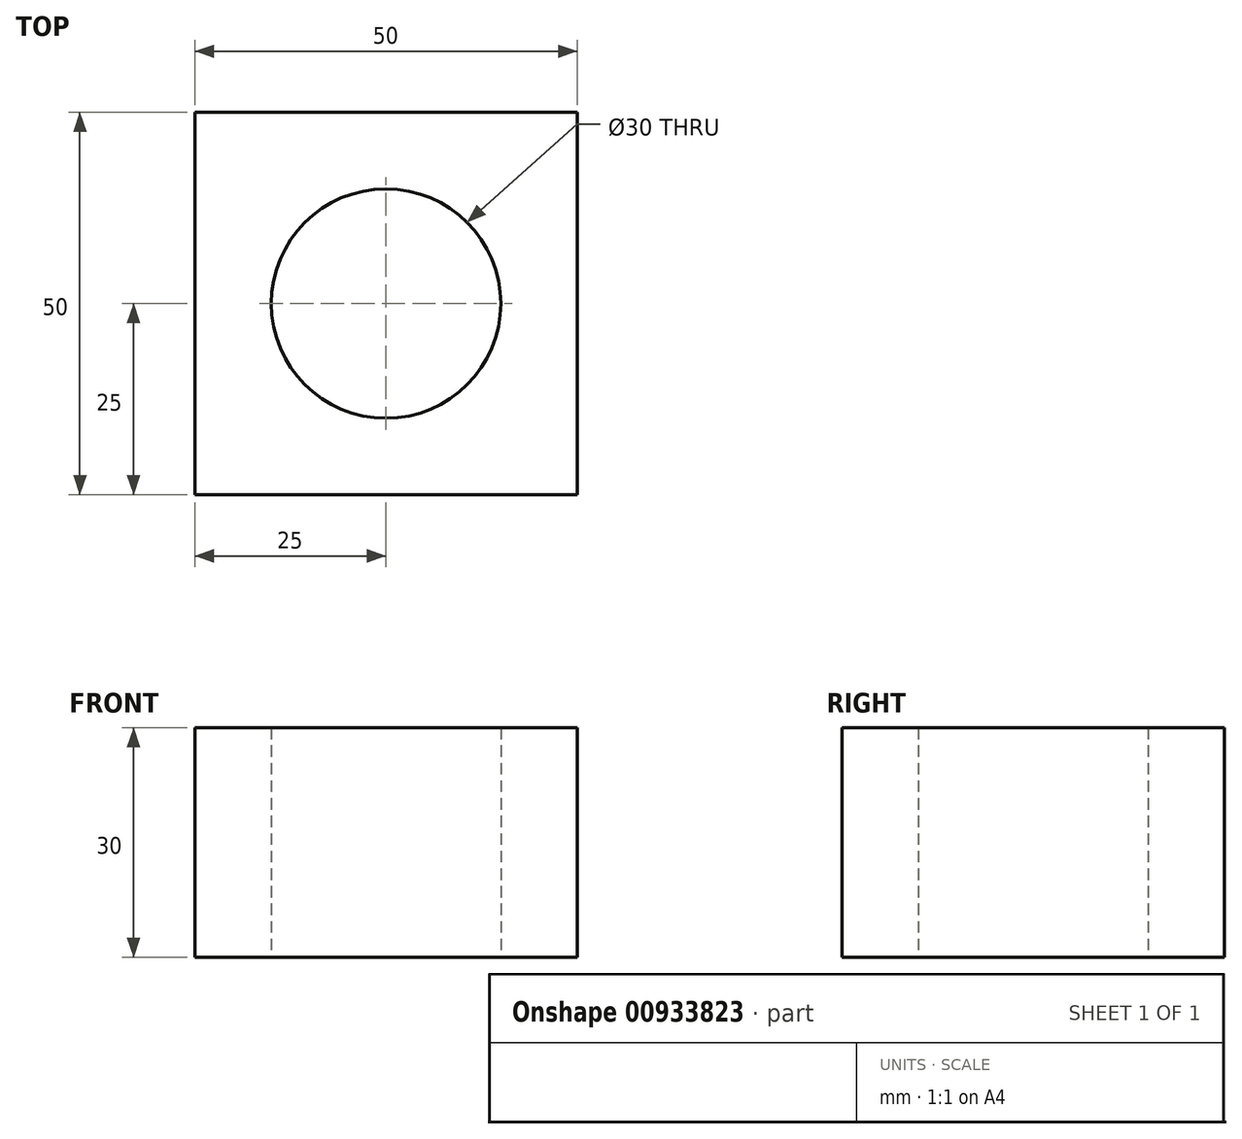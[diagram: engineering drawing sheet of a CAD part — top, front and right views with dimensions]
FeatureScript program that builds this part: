
annotation { "Feature Type Name" : "Feature", "Feature Type Description" : "" }
export const myFeature = defineFeature(function(context is Context, id is Id, definition is map)
    precondition{}
    {
        {
            var Q0;
            Q0=qCreatedBy(makeId("Top.planeOp"),FACE);
            var sketch = newSketch(context, id + "F0", { "sketchPlane" : qUnion([Q0])});
            skLineSegment(sketch, "E0.bottom", {"start": v(-25, 25) * mm, "end": v(25, 25) * mm});
            skLineSegment(sketch, "E0.top", {"start": v(-25, -25) * mm, "end": v(25, -25) * mm});
            skLineSegment(sketch, "E0.left", {"start": v(-25, 25) * mm, "end": v(-25, -25) * mm});
            skLineSegment(sketch, "E0.right", {"start": v(25, 25) * mm, "end": v(25, -25) * mm});
            skPoint(sketch, "E0.middle", {"position": v(0, 0) * mm});
            skCircle(sketch, "E1", {"center": v(0, 0) * mm, "radius": 15 * mm});
            skSolve(sketch);
        }
        {
            var Q0;
            Q0=makeQuery(id+"F0.imprint","IMPRINT",FACE,{"disambiguationData":[TD([[makeQuery(id+"F0.imprint","IMPRINT",EDGE,{"derivedFrom":sQuery(id+"F0.wireOp",EDGE,"E0.bottom")}),-1.0]])]});
            extrude(context, id + "F1", {"entities" : qUnion([Q0]), "depth" : 30 * mm, "offsetDistance" : 25 * mm});
        }
    });
